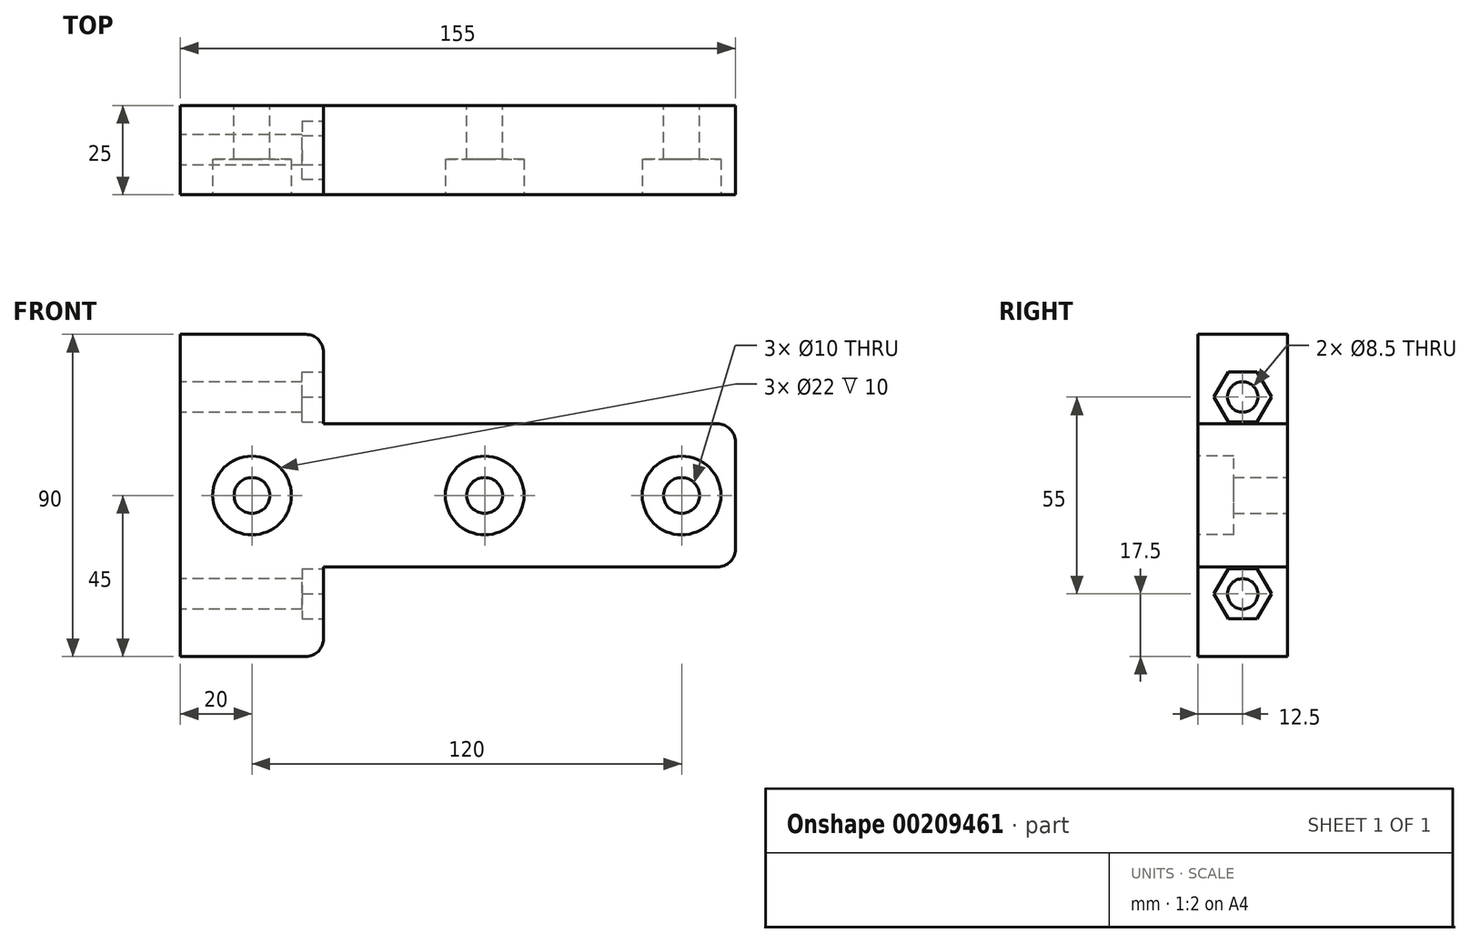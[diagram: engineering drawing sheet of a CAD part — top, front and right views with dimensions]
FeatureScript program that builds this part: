
annotation { "Feature Type Name" : "Feature", "Feature Type Description" : "" }
export const myFeature = defineFeature(function(context is Context, id is Id, definition is map)
    precondition{}
    {
        {
            var Q0;
            Q0=qCreatedBy(makeId("Front.planeOp"),FACE);
            var sketch = newSketch(context, id + "F0", { "sketchPlane" : qUnion([Q0])});
            skLineSegment(sketch, "E0.bottom", {"start": v(70, 20) * mm, "end": v(-85, 20) * mm});
            skLineSegment(sketch, "E0.top", {"start": v(70, -20) * mm, "end": v(-85, -20) * mm});
            skLineSegment(sketch, "E0.right", {"start": v(-85, 20) * mm, "end": v(-85, -20) * mm});
            skPoint(sketch, "E0.middle", {"position": v(0, 0) * mm});
            skCircle(sketch, "E1", {"center": v(0, 0) * mm, "radius": 5 * mm});
            skCircle(sketch, "E2", {"center": v(55, 0) * mm, "radius": 5 * mm});
            skCircle(sketch, "E3", {"center": v(-65, 0) * mm, "radius": 5 * mm});
            skLineSegment(sketch, "E4", {"start": v(70, 20) * mm, "end": v(70, -20) * mm});
            skSolve(sketch);
        }
        {
            var Q0;
            Q0 = qSketchRegion(id + "F0", true);
            extrude(context, id + "F1", {"entities" : qUnion([Q0]), "depth" : 25 * mm});
        }
        {
            var Q0;
            Q0=makeQuery(id+"F1.opExtrude","CAP_FACE",FACE,{"disambiguationData":[OSD([sQuery(id+"F0.wireOp",EDGE,"E0.bottom"),sQuery(id+"F0.wireOp",EDGE,"E0.top"),sQuery(id+"F0.wireOp",EDGE,"E0.right"),sQuery(id+"F0.wireOp",EDGE,"E1"),sQuery(id+"F0.wireOp",EDGE,"E2"),sQuery(id+"F0.wireOp",EDGE,"E3"),sQuery(id+"F0.wireOp",EDGE,"E4")])],"isStart":false});
            var sketch = newSketch(context, id + "F2", { "sketchPlane" : qUnion([Q0])});
            skCircle(sketch, "E5", {"center": v(-65, 0) * mm, "radius": 11 * mm});
            skCircle(sketch, "E6", {"center": v(0, 0) * mm, "radius": 11 * mm});
            skCircle(sketch, "E7", {"center": v(55, 0) * mm, "radius": 11 * mm});
            skSolve(sketch);
        }
        {
            var Q0;
            Q0 = qSketchRegion(id + "F2", true);
            extrude(context, id + "F3", {"entities" : qUnion([Q0]), "operationType" : NewBodyOperationType.REMOVE, "oppositeDirection" : true, "depth" : 10 * mm});
        }
        {
            var Q0;
            Q0=makeQuery(id+"F1.opExtrude","CAP_FACE",FACE,{"disambiguationData":[OSD([sQuery(id+"F0.wireOp",EDGE,"E0.bottom"),sQuery(id+"F0.wireOp",EDGE,"E0.top"),sQuery(id+"F0.wireOp",EDGE,"E0.right"),sQuery(id+"F0.wireOp",EDGE,"E1"),sQuery(id+"F0.wireOp",EDGE,"E2"),sQuery(id+"F0.wireOp",EDGE,"E3"),sQuery(id+"F0.wireOp",EDGE,"E4")])],"isStart":true});
            var sketch = newSketch(context, id + "F4", { "sketchPlane" : qUnion([Q0])});
            skLineSegment(sketch, "E8", {"start": v(45, 20) * mm, "end": v(45, 45) * mm});
            skLineSegment(sketch, "E9", {"start": v(45, 45) * mm, "end": v(85, 45) * mm});
            skLineSegment(sketch, "E10", {"start": v(85, 45) * mm, "end": v(85, 20) * mm});
            skLineSegment(sketch, "E11", {"start": v(85, 20) * mm, "end": v(45, 20) * mm});
            skLineSegment(sketch, "E12", {"start": v(85, -20) * mm, "end": v(85, -45) * mm});
            skLineSegment(sketch, "E13", {"start": v(85, -45) * mm, "end": v(45, -45) * mm});
            skLineSegment(sketch, "E14", {"start": v(45, -45) * mm, "end": v(45, -20) * mm});
            skLineSegment(sketch, "E15", {"start": v(45, -20) * mm, "end": v(85, -20) * mm});
            skSolve(sketch);
        }
        {
            var Q0;
            Q0 = qSketchRegion(id + "F4", true);
            extrude(context, id + "F5", {"entities" : qUnion([Q0]), "operationType" : NewBodyOperationType.ADD, "oppositeDirection" : true, "depth" : 25 * mm});
        }
        {
            var Q0;
            Q0=makeQuery(id+"F5.boolean.opBoolean","MERGE",FACE,{"derivedFrom":[makeQuery(id+"F1.opExtrude","SWEPT_FACE",FACE,{"disambiguationData":[OSD([sQuery(id+"F0.wireOp",EDGE,"E0.right")])]}),makeQuery(id+"F5.opExtrude","SWEPT_FACE",FACE,{"disambiguationData":[OSD([sQuery(id+"F4.wireOp",EDGE,"E10")])]}),makeQuery(id+"F5.opExtrude","SWEPT_FACE",FACE,{"disambiguationData":[OSD([sQuery(id+"F4.wireOp",EDGE,"E12")])]})]});
            var sketch = newSketch(context, id + "F6", { "sketchPlane" : qUnion([Q0])});
            skCircle(sketch, "E16", {"center": v(12.5, 27.5) * mm, "radius": 4.25 * mm});
            skCircle(sketch, "E17", {"center": v(12.5, -27.5) * mm, "radius": 4.25 * mm});
            skSolve(sketch);
        }
        {
            var Q0;
            Q0 = qSketchRegion(id + "F6", true);
            extrude(context, id + "F7", {"entities" : qUnion([Q0]), "operationType" : NewBodyOperationType.REMOVE, "endBound" : BoundingType.UP_TO_NEXT, "oppositeDirection" : true, "depth" : 25 * mm});
        }
        {
            var Q0;
            Q0=makeQuery(id+"F5.opExtrude","SWEPT_FACE",FACE,{"disambiguationData":[OSD([sQuery(id+"F4.wireOp",EDGE,"E8")])]});
            var sketch = newSketch(context, id + "F8", { "sketchPlane" : qUnion([Q0])});
            skCircle(sketch, "E18.cCircle", {"center": v(-12.5, 27.5) * mm, "radius": 7 * mm, "construction": true});
            skLineSegment(sketch, "E18.0", {"start": v(-16.54, 34.5) * mm, "end": v(-8.46, 34.5) * mm});
            skLineSegment(sketch, "E18.1", {"start": v(-8.46, 34.5) * mm, "end": v(-4.42, 27.5) * mm});
            skLineSegment(sketch, "E18.2", {"start": v(-4.42, 27.5) * mm, "end": v(-8.46, 20.5) * mm});
            skLineSegment(sketch, "E18.3", {"start": v(-8.46, 20.5) * mm, "end": v(-16.54, 20.5) * mm});
            skLineSegment(sketch, "E18.4", {"start": v(-16.54, 20.5) * mm, "end": v(-20.58, 27.5) * mm});
            skLineSegment(sketch, "E18.5", {"start": v(-20.58, 27.5) * mm, "end": v(-16.54, 34.5) * mm});
            skPoint(sketch, "E18.0.midPoint", {"position": v(-12.5, 34.5) * mm});
            skLineSegment(sketch, "E19.MirrorCS", {"start": v(-16.54, -20.5) * mm, "end": v(-20.58, -27.5) * mm});
            skLineSegment(sketch, "E20.MirrorCS", {"start": v(-8.46, -20.5) * mm, "end": v(-16.54, -20.5) * mm});
            skLineSegment(sketch, "E21.MirrorCS", {"start": v(-4.42, -27.5) * mm, "end": v(-8.46, -20.5) * mm});
            skLineSegment(sketch, "E22.MirrorCS", {"start": v(-8.46, -34.5) * mm, "end": v(-4.42, -27.5) * mm});
            skLineSegment(sketch, "E23.MirrorCS", {"start": v(-20.58, -27.5) * mm, "end": v(-16.54, -34.5) * mm});
            skLineSegment(sketch, "E24.MirrorCS", {"start": v(-16.54, -34.5) * mm, "end": v(-8.46, -34.5) * mm});
            skSolve(sketch);
        }
        {
            var Q0;
            Q0 = qSketchRegion(id + "F8", true);
            extrude(context, id + "F9", {"entities" : qUnion([Q0]), "operationType" : NewBodyOperationType.REMOVE, "oppositeDirection" : true, "depth" : 6 * mm});
        }
        {
            var Q0;
            Q0=makeQuery(id+"F5.opExtrude","SWEPT_EDGE",EDGE,{"disambiguationData":[OSD([sQuery(id+"F0.wireOp",EDGE,"E0.bottom"),sQuery(id+"F4.wireOp",EDGE,"E8"),sQuery(id+"F4.wireOp",EDGE,"E11")])]});
            var Q1;
            Q1=makeQuery(id+"F5.opExtrude","SWEPT_EDGE",EDGE,{"disambiguationData":[OSD([sQuery(id+"F4.wireOp",EDGE,"E8"),sQuery(id+"F4.wireOp",EDGE,"E9")])]});
            var Q2;
            Q2=makeQuery(id+"F5.opExtrude","SWEPT_EDGE",EDGE,{"disambiguationData":[OSD([sQuery(id+"F0.wireOp",EDGE,"E0.top"),sQuery(id+"F4.wireOp",EDGE,"E14"),sQuery(id+"F4.wireOp",EDGE,"E15")])]});
            var Q3;
            Q3=makeQuery(id+"F5.opExtrude","SWEPT_EDGE",EDGE,{"disambiguationData":[OSD([sQuery(id+"F4.wireOp",EDGE,"E13"),sQuery(id+"F4.wireOp",EDGE,"E14")])]});
            var Q4;
            Q4=makeQuery(id+"F1.opExtrude","SWEPT_EDGE",EDGE,{"disambiguationData":[OSD([sQuery(id+"F0.wireOp",EDGE,"E0.top"),sQuery(id+"F0.wireOp",EDGE,"E4")])]});
            var Q5;
            Q5=makeQuery(id+"F1.opExtrude","SWEPT_EDGE",EDGE,{"disambiguationData":[OSD([sQuery(id+"F0.wireOp",EDGE,"E0.bottom"),sQuery(id+"F0.wireOp",EDGE,"E4")])]});
            fillet(context, id + "F10", {"entities" : qUnion([Q0, Q1, Q2, Q3, Q4, Q5]), "radius" : 5 * mm, "tangentPropagation" : true, "allowEdgeOverflow" : false});
        }
    });
